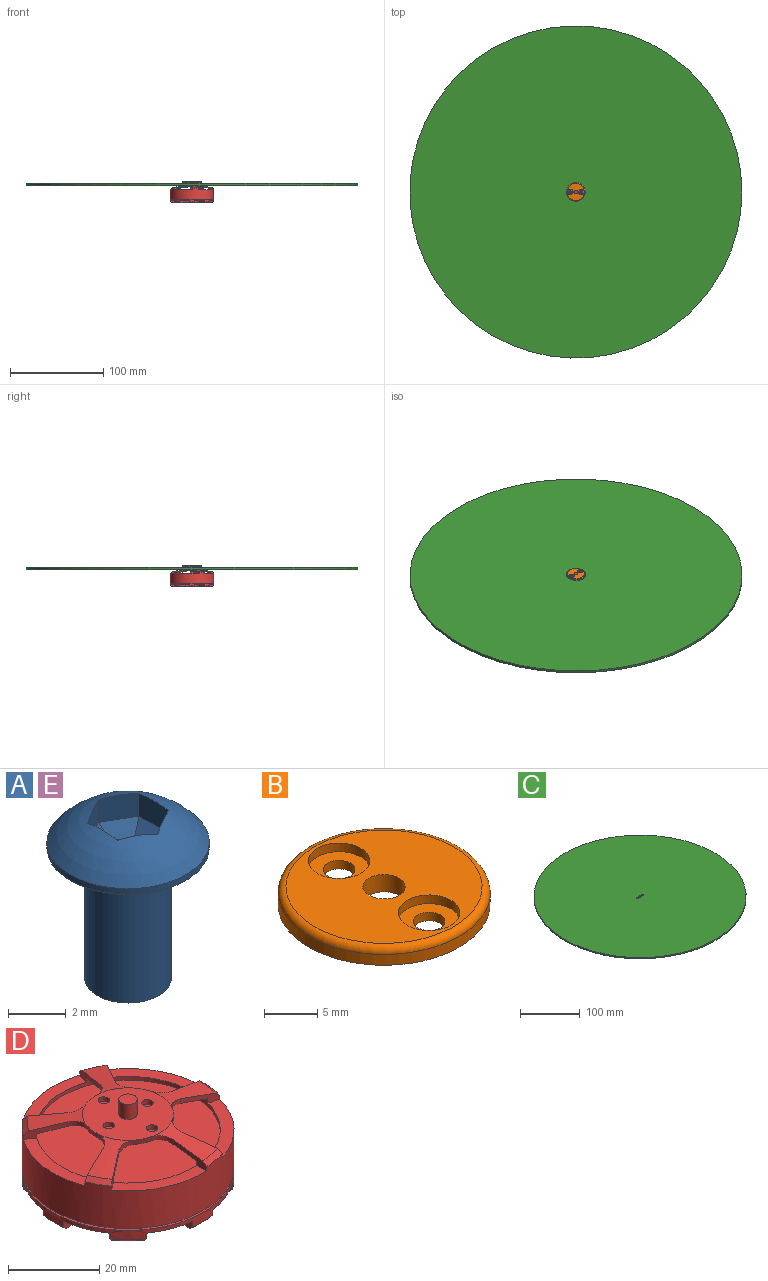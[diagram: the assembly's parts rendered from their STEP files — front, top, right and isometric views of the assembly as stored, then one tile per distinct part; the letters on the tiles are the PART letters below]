
ASSEMBLY  parts=5 mates=12
PART A: 18 faces, bbox 5.6x5.6x6.9 mm
  f0: sphere r=3.58mm, area 24.7mm2, adj f4,f5,f6,f7,f8,f9,f10
  f1: plane 3x3mm, normal (0,0,-1), area 7.1mm2, adj f2
  f2: cylinder r=1.5mm len=5.5mm, axis (0,0,1), area 51.8mm2, adj f1,f3
  f3: plane 5.6x5.6mm, normal (0,0,-1), area 17.6mm2, adj f2,f4
  f4: cylinder r=2.8mm len=5.6mm, axis (0,0,1), area 4.4mm2, adj f0,f3
  f5: plane 1.44x1.02mm, normal (-1,0,0), area 1.4mm2, adj f0,f6,f10,f17
  f6: plane 1.25x1.02mm, normal (-0.5,-0.87,0), area 1.4mm2, adj f0,f5,f7,f15
  f7: plane 1.25x1.02mm, normal (0.5,-0.87,0), area 1.4mm2, adj f0,f6,f8,f13
  f8: plane 1.44x1.02mm, normal (1,0,0), area 1.4mm2, adj f0,f7,f9,f12
  f9: plane 1.25x1.02mm, normal (0.5,0.87,0), area 1.4mm2, adj f0,f8,f10,f14
  f10: plane 1.25x1.02mm, normal (-0.5,0.87,0), area 1.4mm2, adj f0,f5,f9,f16
  f11: plane 1.73x1.5mm, normal (0,0,1), area 1.9mm2, adj f12,f13,f14,f15,f16,f17
  f12: plane 1.44x0.5mm, normal (0.71,0,0.71), area 0.8mm2, adj f8,f11,f13,f14
  f13: plane 1.25x1.01mm, normal (0.35,-0.61,0.71), area 0.8mm2, adj f7,f11,f12,f15
  f14: plane 1.25x1.01mm, normal (0.35,0.61,0.71), area 0.8mm2, adj f9,f11,f12,f16
  f15: plane 1.25x1.01mm, normal (-0.35,-0.61,0.71), area 0.8mm2, adj f6,f11,f13,f17
  f16: plane 1.25x1.01mm, normal (-0.35,0.61,0.71), area 0.8mm2, adj f10,f11,f14,f17
  f17: plane 1.44x0.5mm, normal (-0.71,0,0.71), area 0.8mm2, adj f5,f11,f15,f16
PART B: 11 faces, bbox 21.6x21.6x2 mm
  f0: plane 5.8x5.8mm, normal (0,0,1), area 19.4mm2, adj f5,f8
  f1: plane 5.8x5.8mm, normal (0,0,1), area 19.4mm2, adj f2,f7
  f2: cylinder r=1.5mm len=3mm, axis (0,0,1), area 9.4mm2, adj f1,f6
  f3: cylinder r=10mm len=20mm, axis (0,0,1), area 78.5mm2, adj f6,f10
  f4: cylinder r=2mm len=4mm, axis (0,0,1), area 25.1mm2, adj f6,f9
  f5: cylinder r=1.5mm len=3mm, axis (0,0,1), area 9.4mm2, adj f0,f6
  f6: plane 20x20mm, normal (0,0,-1), area 287.5mm2, adj f2,f3,f4,f5
  f7: cylinder r=2.9mm len=5.8mm, axis (0,0,-1), area 18.2mm2, adj f1,f9
  f8: cylinder r=2.9mm len=5.8mm, axis (0,0,-1), area 18.2mm2, adj f0,f9
  f9: plane 18.5x18.5mm, normal (0,0,1), area 203.4mm2, adj f4,f7,f8,f10
  f10: torus R=9.25mm, axis (0,0,1), area 72mm2, adj f3,f9
PART C: 6 faces, bbox 355.6x355.6x2.5 mm
  f0: cylinder r=1.5mm len=3mm, axis (0,0,-1), area 23.6mm2, adj f4,f5
  f1: cylinder r=1.5mm len=3mm, axis (0,0,-1), area 23.6mm2, adj f4,f5
  f2: cylinder r=2mm len=4mm, axis (0,0,-1), area 31.4mm2, adj f4,f5
  f3: cylinder r=177.8mm len=355.6mm, axis (0,0,-1), area 2792.9mm2, adj f4,f5
  f4: plane 355.6x355.6mm, normal (0,0,1), area 99288mm2, adj f0,f1,f2,f3
  f5: plane 355.6x355.6mm, normal (0,0,-1), area 99288mm2, adj f0,f1,f2,f3
PART D: 121 faces, bbox 46.5x46.5x34.8 mm
  f0: plane 44.5x44.16mm, normal (0,0,-1), area 795.6mm2, adj f1,f2,f3,f4,f5,f6,f7,f8
  f1: cone r=22.25mm half-angle=45deg, axis (0,0,1), area 5.6mm2, adj f0,f16,f108,f111
  f2: cone r=22.25mm half-angle=45deg, axis (0,0,1), area 11.2mm2, adj f0,f16,f104,f107
  f3: cone r=22.25mm half-angle=45deg, axis (0,0,1), area 8.4mm2, adj f0,f16,f100,f103
  f4: cone r=22.25mm half-angle=45deg, axis (0,0,1), area 8.4mm2, adj f0,f16,f76,f95
  f5: cone r=22.25mm half-angle=45deg, axis (0,0,1), area 11.2mm2, adj f0,f16,f96,f99
  f6: cone r=22.25mm half-angle=45deg, axis (0,0,1), area 11.2mm2, adj f0,f16,f88,f91
  f7: cone r=22.25mm half-angle=45deg, axis (0,0,1), area 8.4mm2, adj f0,f16,f80,f87
  f8: cone r=22.25mm half-angle=45deg, axis (0,0,1), area 5.6mm2, adj f0,f16,f83,f92
  f9: cone r=22.25mm half-angle=45deg, axis (0,0,1), area 11.2mm2, adj f0,f16,f75,f79
  f10: plane 9.64x3.6mm, normal (-0.26,-0.97,0), area 14.3mm2, adj f12,f20,f22,f23,f26,f35,f72
  f11: plane 9.98x3.6mm, normal (0,1,0), area 14.3mm2, adj f12,f20,f22,f23,f26,f28,f73
  f12: cone r=22.05mm half-angle=80deg, axis (0,0,-1), area 62.4mm2, adj f10,f11,f13,f26,f72,f73
  f13: plane 20x20mm, normal (0,0,1), area 282mm2, adj f12,f14,f27,f31,f34,f38,f41,f45
  f14: cylinder r=2mm len=4mm, axis (0,0,1), area 50.3mm2, adj f13,f15
  f15: plane 4x4mm, normal (0,0,1), area 12.6mm2, adj f14
  f16: cylinder r=23.25mm len=46.5mm, axis (0,0,1), area 234.3mm2, adj f1,f2,f3,f4,f5,f6,f7,f8
  f17: plane 46.5x46.5mm, normal (0,0,1), area 212.1mm2, adj f16,f18
  f18: cylinder r=21.75mm len=43.5mm, axis (0,0,1), area 68.3mm2, adj f17,f19
  f19: plane 46.5x46.5mm, normal (0,0,-1), area 212.1mm2, adj f18,f20
  f20: cylinder r=23.25mm len=46.5mm, axis (0,0,1), area 1508mm2, adj f10,f11,f19,f26,f28,f29,f30,f33
  f21: plane 19.79x19.79mm, normal (0,0,-1), area 275.4mm2, adj f22,f25,f27,f32,f34,f39,f41,f46
  f22: cone r=20.25mm half-angle=80deg, axis (0,0,-1), area 52.5mm2, adj f10,f11,f21,f23,f72,f73
  f23: cylinder r=20.25mm len=40.5mm, axis (0,0,1), area 158.4mm2, adj f10,f11,f22,f24,f28,f29,f30,f32
  f24: plane 40.5x40.5mm, normal (0,0,1), area 1275.7mm2, adj f23,f25
  f25: cylinder r=2mm len=4mm, axis (0,0,1), area 50.3mm2, adj f21,f24
  f26: cone r=22.05mm half-angle=50deg, axis (0,0,-1), area 9.3mm2, adj f10,f11,f12,f20
  f27: cone r=10mm half-angle=5deg, axis (0,0,1), area 4.9mm2, adj f13,f21,f73,f74
  f28: plane 19.5x12.22mm, normal (0,0,1), area 64.9mm2, adj f11,f20,f23,f54
  f29: plane 9.97x3.6mm, normal (-1,-0.05,0), area 14.3mm2, adj f20,f23,f31,f32,f33,f42,f70
  f30: plane 9.49x3.6mm, normal (0.95,0.31,0), area 14.3mm2, adj f20,f23,f31,f32,f33,f35,f71
  f31: cone r=22.05mm half-angle=80deg, axis (0,0,-1), area 62.4mm2, adj f13,f29,f30,f33,f70,f71
  f32: cone r=20.25mm half-angle=80deg, axis (0,0,-1), area 52.5mm2, adj f21,f23,f29,f30,f70,f71
  f33: cone r=22.05mm half-angle=50deg, axis (0,0,-1), area 9.3mm2, adj f20,f29,f30,f31
  f34: cone r=10mm half-angle=5deg, axis (0,0,1), area 4.9mm2, adj f13,f21,f71,f72
  f35: plane 16.87x16.2mm, normal (0,0,1), area 64.9mm2, adj f10,f20,f23,f30
  f36: plane 9.32x3.6mm, normal (-0.36,0.93,0), area 14.3mm2, adj f20,f23,f38,f39,f40,f49,f68
  f37: plane 8.08x5.87mm, normal (0.59,-0.81,0), area 14.3mm2, adj f20,f23,f38,f39,f40,f42,f69
  f38: cone r=22.05mm half-angle=80deg, axis (0,0,-1), area 62.4mm2, adj f13,f36,f37,f40,f68,f69
  f39: cone r=20.25mm half-angle=80deg, axis (0,0,-1), area 52.5mm2, adj f21,f23,f36,f37,f68,f69
  f40: cone r=22.05mm half-angle=50deg, axis (0,0,-1), area 9.3mm2, adj f20,f36,f37,f38
  f41: cone r=10mm half-angle=5deg, axis (0,0,1), area 4.9mm2, adj f13,f21,f69,f70
  f42: plane 20.03x11.35mm, normal (0,0,1), area 64.9mm2, adj f20,f23,f29,f37
  f43: plane 7.76x6.28mm, normal (0.78,0.63,0), area 14.3mm2, adj f20,f23,f45,f46,f47,f56,f66
  f44: plane 8.08x5.87mm, normal (-0.59,-0.81,0), area 14.3mm2, adj f20,f23,f45,f46,f47,f49,f67
  f45: cone r=22.05mm half-angle=80deg, axis (0,0,-1), area 62.4mm2, adj f13,f43,f44,f47,f66,f67
  f46: cone r=20.25mm half-angle=80deg, axis (0,0,-1), area 52.5mm2, adj f21,f23,f43,f44,f66,f67
  f47: cone r=22.05mm half-angle=50deg, axis (0,0,-1), area 9.3mm2, adj f20,f43,f44,f45
  f48: cone r=10mm half-angle=5deg, axis (0,0,1), area 4.9mm2, adj f13,f21,f67,f68
  f49: plane 22x6.87mm, normal (0,0,1), area 64.9mm2, adj f20,f23,f36,f44
  f50: plane 9.49x3.6mm, normal (-0.95,0.31,0), area 14.3mm2, adj f20,f23,f51,f52,f53,f56,f65
  f51: cone r=22.05mm half-angle=80deg, axis (0,0,-1), area 62.4mm2, adj f13,f50,f53,f54,f65,f74
  f52: cone r=20.25mm half-angle=80deg, axis (0,0,-1), area 52.5mm2, adj f21,f23,f50,f54,f65,f74
  f53: cone r=22.05mm half-angle=50deg, axis (0,0,-1), area 9.3mm2, adj f20,f50,f51,f54
  f54: plane 8.37x5.44mm, normal (0.84,-0.54,0), area 14.3mm2, adj f20,f23,f28,f51,f52,f53,f74
  f55: cone r=10mm half-angle=5deg, axis (0,0,1), area 4.9mm2, adj f13,f21,f65,f66
  f56: plane 21.82x7.51mm, normal (0,0,1), area 64.9mm2, adj f20,f23,f43,f50
  f57: cylinder r=1.5mm len=5mm, axis (0,0,-1), area 47.1mm2, adj f0,f58
  f58: plane 3x3mm, normal (0,0,-1), area 7.1mm2, adj f57
  f59: cylinder r=1.5mm len=5mm, axis (0,0,-1), area 47.1mm2, adj f0,f60
  f60: plane 3x3mm, normal (0,0,-1), area 7.1mm2, adj f59
  f61: cylinder r=1.5mm len=5mm, axis (0,0,-1), area 47.1mm2, adj f0,f62
  f62: plane 3x3mm, normal (0,0,-1), area 7.1mm2, adj f61
  f63: cylinder r=1.5mm len=5mm, axis (0,0,-1), area 47.1mm2, adj f0,f64
  f64: plane 3x3mm, normal (0,0,-1), area 7.1mm2, adj f63
  f65: bspline ~20.1x4.52mm, area 6.2mm2, adj f50,f51,f52,f55
  f66: bspline ~34.39x6.45mm, area 6.2mm2, adj f43,f45,f46,f55
  f67: bspline ~20.1x5.59mm, area 6.2mm2, adj f44,f45,f46,f48
  f68: bspline ~34.39x5.58mm, area 6.2mm2, adj f36,f38,f39,f48
  f69: bspline ~20.1x6.21mm, area 6.2mm2, adj f37,f38,f39,f41
  f70: bspline ~34.39x6.73mm, area 6.2mm2, adj f29,f31,f32,f41
  f71: bspline ~20.1x6.21mm, area 6.2mm2, adj f30,f31,f32,f34
  f72: bspline ~34.39x7.35mm, area 6.2mm2, adj f10,f12,f22,f34
  f73: bspline ~20.1x5.61mm, area 6.2mm2, adj f11,f12,f22,f27
  f74: bspline ~34.39x7.26mm, area 6.2mm2, adj f27,f51,f52,f54
  f75: plane 9x6.3mm, normal (-0.57,0.82,0), area 27mm2, adj f0,f9,f16,f77,f78
  f76: plane 10.9x2.5mm, normal (0.13,-0.99,0), area 27mm2, adj f0,f4,f16,f77,f78
  f77: cylinder r=3mm len=5.46mm, axis (0,0,-1), area 20mm2, adj f0,f75,f76,f78
  f78: plane 14.29x11.76mm, normal (0,0,-1), area 104.9mm2, adj f16,f75,f76,f77
  f79: plane 9x6.3mm, normal (0.82,-0.57,0), area 27mm2, adj f0,f9,f16,f81,f82
  f80: plane 10.9x2.5mm, normal (-0.99,0.13,0), area 27mm2, adj f0,f7,f16,f81,f82
  f81: cylinder r=3mm len=5.46mm, axis (0,0,-1), area 20mm2, adj f0,f79,f80,f82
  f82: plane 14.29x11.76mm, normal (0,0,-1), area 104.9mm2, adj f16,f79,f80,f81
  f83: plane 2.5x1.17mm, normal (0.17,0.98,0), area 2.5mm2, adj f0,f8,f16,f85,f86
  f84: plane 2.5x1.75mm, normal (1,0,0), area 4.4mm2, adj f0,f85,f86,f112
  f85: cylinder r=3mm len=2.95mm, axis (0,0,-1), area 10.5mm2, adj f0,f83,f84,f86
  f86: plane 8.07x4mm, normal (0,0,-1), area 26.5mm2, adj f16,f83,f84,f85,f111,f112
  f87: plane 10.92x2.5mm, normal (0.99,0.13,0), area 27mm2, adj f0,f7,f16,f89,f90
  f88: plane 9.02x6.32mm, normal (-0.82,-0.57,0), area 27mm2, adj f0,f6,f16,f89,f90
  f89: cylinder r=3mm len=5.46mm, axis (0,0,-1), area 20mm2, adj f0,f87,f88,f90
  f90: plane 14.31x11.77mm, normal (0,0,-1), area 105.2mm2, adj f16,f87,f88,f89
  f91: plane 9.09x6.37mm, normal (0.57,0.82,0), area 27.2mm2, adj f0,f6,f16,f93,f94
  f92: plane 10.43x3.8mm, normal (-0.34,-0.94,0), area 27.2mm2, adj f0,f8,f16,f93,f94
  f93: cylinder r=1.6mm len=2.91mm, axis (0,0,-1), area 11.5mm2, adj f0,f91,f92,f94
  f94: plane 12.58x9.28mm, normal (0,0,-1), area 55mm2, adj f16,f91,f92,f93
  f95: plane 10.9x2.5mm, normal (0.13,0.99,0), area 27mm2, adj f0,f4,f16,f97,f98
  f96: plane 9x6.3mm, normal (-0.57,-0.82,0), area 27mm2, adj f0,f5,f16,f97,f98
  f97: cylinder r=3mm len=5.46mm, axis (0,0,-1), area 20mm2, adj f0,f95,f96,f98
  f98: plane 14.29x11.76mm, normal (0,0,-1), area 104.9mm2, adj f16,f95,f96,f97
  f99: plane 9x6.3mm, normal (0.82,0.57,0), area 27mm2, adj f0,f5,f16,f101,f102
  f100: plane 10.9x2.5mm, normal (-0.99,-0.13,0), area 27mm2, adj f0,f3,f16,f101,f102
  f101: cylinder r=3mm len=5.46mm, axis (0,0,-1), area 20mm2, adj f0,f99,f100,f102
  f102: plane 14.29x11.76mm, normal (0,0,-1), area 104.9mm2, adj f16,f99,f100,f101
  f103: plane 10.92x2.5mm, normal (0.99,-0.13,0), area 27mm2, adj f0,f3,f16,f105,f106
  f104: plane 9.02x6.32mm, normal (-0.82,0.57,0), area 27mm2, adj f0,f2,f16,f105,f106
  f105: cylinder r=3mm len=5.46mm, axis (0,0,-1), area 20mm2, adj f0,f103,f104,f106
  f106: plane 14.31x11.77mm, normal (0,0,-1), area 105.2mm2, adj f16,f103,f104,f105
  f107: plane 9.09x6.37mm, normal (0.57,-0.82,0), area 27.2mm2, adj f0,f2,f16,f109,f110
  f108: plane 10.43x3.8mm, normal (-0.34,0.94,0), area 27.2mm2, adj f0,f1,f16,f109,f110
  f109: cylinder r=1.6mm len=2.91mm, axis (0,0,-1), area 11.5mm2, adj f0,f107,f108,f110
  f110: plane 12.58x9.28mm, normal (0,0,-1), area 55mm2, adj f16,f107,f108,f109
  f111: plane 2.5x1.17mm, normal (0.17,-0.98,0), area 2.5mm2, adj f0,f1,f16,f86,f112
  f112: cylinder r=3mm len=2.95mm, axis (0,0,-1), area 10.5mm2, adj f0,f84,f86,f111
  f113: cylinder r=2mm len=4mm, axis (0,0,-1), area 4.4mm2, adj f115,f116
  f114: cylinder r=4mm len=8mm, axis (0,0,-1), area 8.8mm2, adj f0,f115
  f115: plane 8x8mm, normal (0,0,-1), area 37.7mm2, adj f113,f114
  f116: plane 4x4mm, normal (0,0,-1), area 12.6mm2, adj f113
  f117: cylinder r=1.25mm len=2.5mm, axis (0,0,1), area 9.4mm2, adj f13,f21
  f118: cylinder r=1.25mm len=2.5mm, axis (0,0,1), area 9.4mm2, adj f13,f21
  f119: cylinder r=1.25mm len=2.5mm, axis (0,0,1), area 9.4mm2, adj f13,f21
  f120: cylinder r=1.25mm len=2.5mm, axis (0,0,1), area 9.4mm2, adj f13,f21
PART E: same geometry as A
PLACE A t=(-16.2,6.35,24.9)mm
PLACE B rot(axis=(0,0,1),90deg) t=(-10.2,6.35,24.9)mm
PLACE C t=(-10.2,6.35,21.4)mm
PLACE D t=(-10.2,6.35,3.1)mm fixed
PLACE E t=(-4.2,6.35,24.9)mm
MATE planar B.f3 <-> C.f3  axis (0,0,-1) through (-10.2,6.35,23.9)mm
MATE planar A.f2 <-> B.f7  axis (0,0,-1) through (-16.2,6.35,24.9)mm
MATE cylindrical E.f2 <-> B.f5  axis (0,0,1) through (-4.2,6.35,22.15)mm
MATE parallel E.f5 <-> D.f84  axis (-1,0,0) through (-2.95,6.35,25.75)mm
MATE cylindrical B.f4 <-> D.f1  axis (0,0,1) through (-10.2,6.35,25.9)mm
MATE cylindrical B.f5 <-> C.f1  axis (0,0,1) through (-4.2,6.35,24.9)mm
MATE planar C.f3 <-> D.f1  axis (0,0,-1) through (-10.2,6.35,21.4)mm
MATE cylindrical C.f2 <-> D.f1  axis (0,0,-1) through (-10.2,6.35,22.65)mm
MATE cylindrical A.f2 <-> B.f2  axis (0,0,1) through (-16.2,6.35,22.15)mm
MATE planar E.f2 <-> B.f5  axis (0,0,-1) through (-4.2,6.35,24.9)mm
MATE parallel A.f5 <-> D.f84  axis (-1,0,0) through (-14.95,6.35,25.75)mm
MATE cylindrical C.f1 <-> D.f120  axis (0,0,-1) through (-4.2,6.35,22.65)mm
